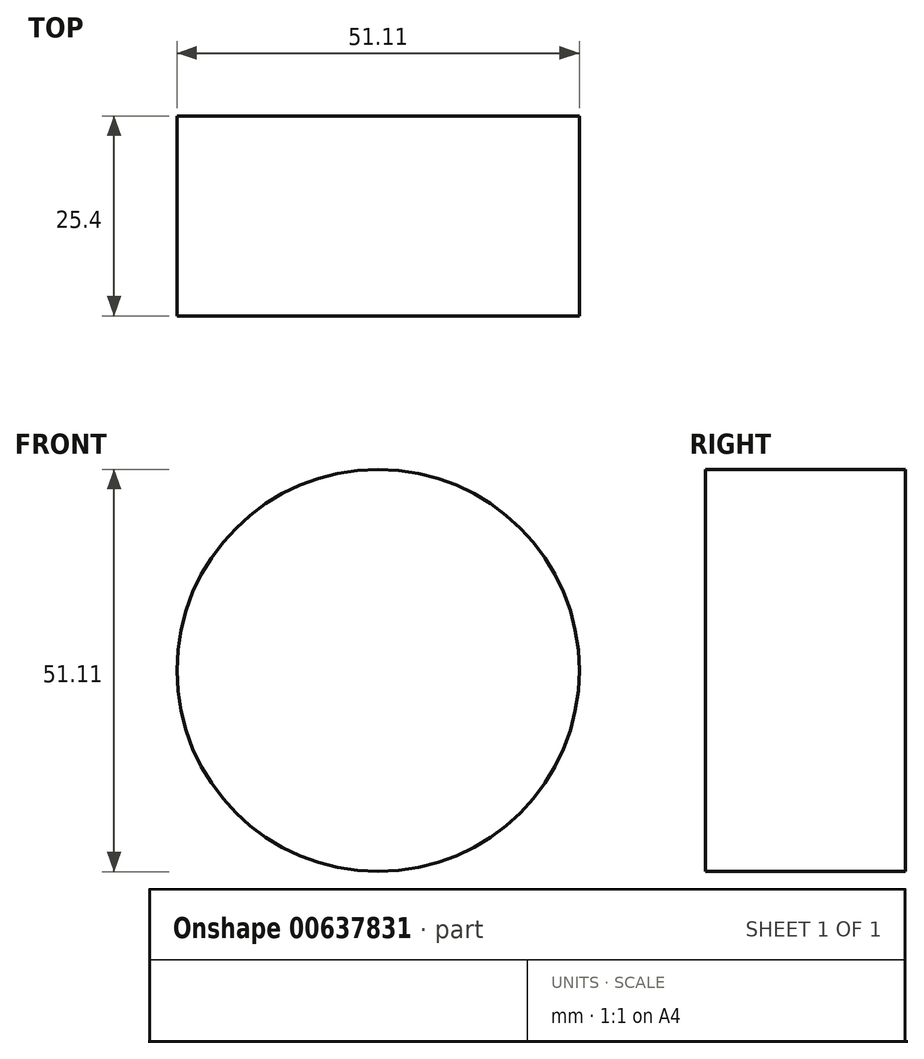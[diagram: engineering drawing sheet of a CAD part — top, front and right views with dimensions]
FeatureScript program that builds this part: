
annotation { "Feature Type Name" : "Feature", "Feature Type Description" : "" }
export const myFeature = defineFeature(function(context is Context, id is Id, definition is map)
    precondition{}
    {
        {
            var Q0;
            Q0=qCreatedBy(makeId("Front.planeOp"),FACE);
            var sketch = newSketch(context, id + "F0", { "sketchPlane" : qUnion([Q0])});
            skCircle(sketch, "E0", {"center": v(-30.27, 50.13) * mm, "radius": 25.55 * mm});
            skSolve(sketch);
        }
        {
            var Q0;
            Q0=makeQuery(id+"F0.imprint","IMPRINT",FACE,{"disambiguationData":[TD([[makeQuery(id+"F0.imprint","IMPRINT",EDGE,{"derivedFrom":sQuery(id+"F0.wireOp",EDGE,"E0")}),1.0]])]});
            extrude(context, id + "F1", {"entities" : qUnion([Q0]), "depth" : 25.4 * mm, "offsetDistance" : 25.4 * mm});
        }
    });
